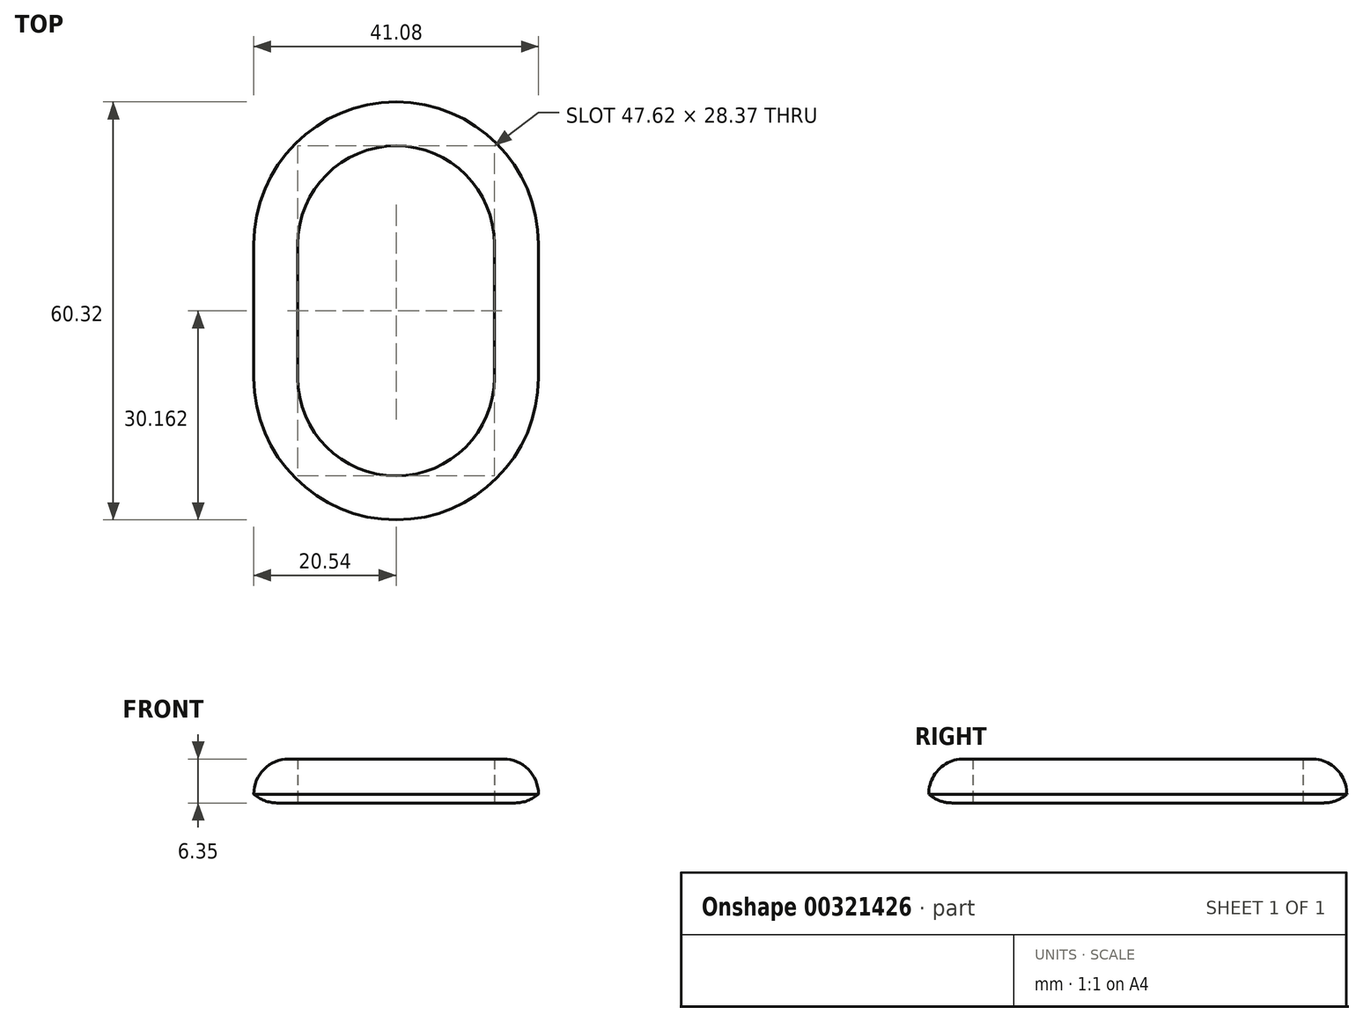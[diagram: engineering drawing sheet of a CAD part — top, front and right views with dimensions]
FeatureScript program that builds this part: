
annotation { "Feature Type Name" : "Feature", "Feature Type Description" : "" }
export const myFeature = defineFeature(function(context is Context, id is Id, definition is map)
    precondition{}
    {
        {
            var Q0;
            Q0=qCreatedBy(makeId("Top.planeOp"),FACE);
            var sketch = newSketch(context, id + "F0", { "sketchPlane" : qUnion([Q0])});
            skArc(sketch, "E0", {"start": v(-14.19, 0) * mm, "mid": v(0, -14.19) * mm, "end": v(14.19, 0) * mm});
            skPoint(sketch, "E1", {"position": v(-14.19, 0) * mm});
            skPoint(sketch, "E2", {"position": v(14.19, 0) * mm});
            skArc(sketch, "E3", {"start": v(14.19, 19.24) * mm, "mid": v(0, 33.43) * mm, "end": v(-14.19, 19.24) * mm});
            skLineSegment(sketch, "E4", {"start": v(-14.19, 19.24) * mm, "end": v(-14.19, 0) * mm});
            skLineSegment(sketch, "E5", {"start": v(14.19, 19.24) * mm, "end": v(14.19, 0) * mm});
            skArc(sketch, "E6.0", {"start": v(20.54, 19.24) * mm, "mid": v(0, 39.78) * mm, "end": v(-20.54, 19.24) * mm});
            skLineSegment(sketch, "E6.1", {"start": v(20.54, 19.24) * mm, "end": v(20.54, 0) * mm});
            skArc(sketch, "E6.2", {"start": v(-20.54, 0) * mm, "mid": v(0, -20.54) * mm, "end": v(20.54, 0) * mm});
            skLineSegment(sketch, "E6.3", {"start": v(-20.54, 19.24) * mm, "end": v(-20.54, 0) * mm});
            skSolve(sketch);
        }
        {
            var Q0;
            Q0 = qSketchRegion(id + "F0", true);
            extrude(context, id + "F1", {"entities" : qUnion([Q0]), "depth" : 6.35 * mm});
        }
        {
            var Q0;
            Q0=makeQuery(id+"F1.opExtrude","CAP_EDGE",EDGE,{"disambiguationData":[OSD([sQuery(id+"F0.wireOp",EDGE,"E6.0")])],"isStart":false});
            fillet(context, id + "F2", {"entities" : qUnion([Q0]), "radius" : 5.08 * mm, "tangentPropagation" : true, "allowEdgeOverflow" : false});
        }
        {
            var Q0;
            Q0=makeQuery(id+"F1.opExtrude","CAP_EDGE",EDGE,{"disambiguationData":[OSD([sQuery(id+"F0.wireOp",EDGE,"E6.0")])],"isStart":true});
            fillet(context, id + "F3", {"entities" : qUnion([Q0]), "radius" : 5.08 * mm, "tangentPropagation" : true, "allowEdgeOverflow" : false});
        }
    });
